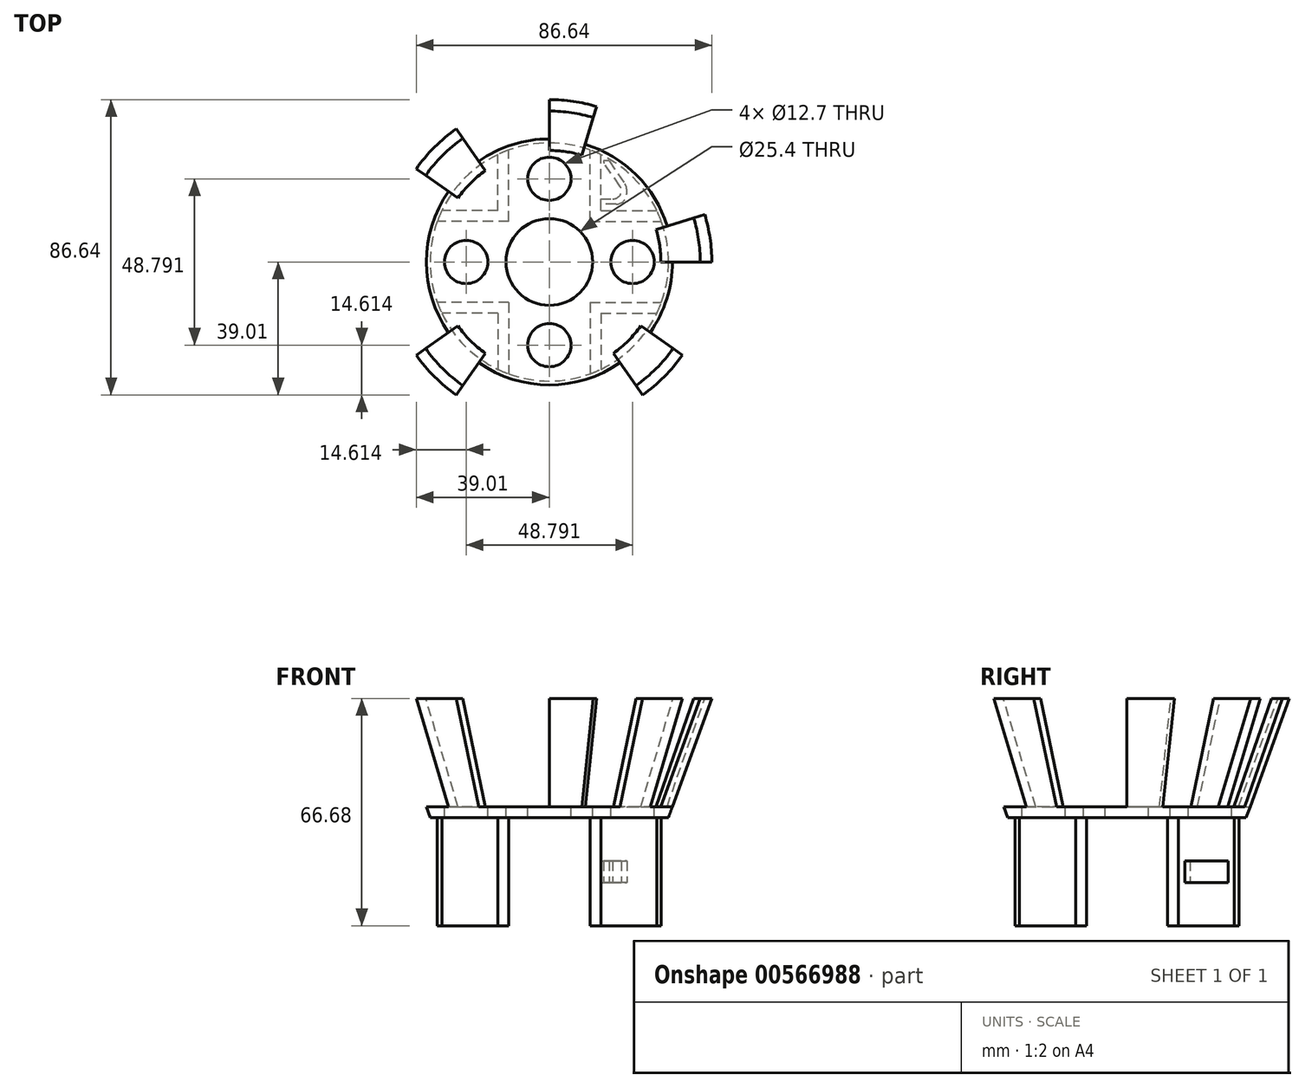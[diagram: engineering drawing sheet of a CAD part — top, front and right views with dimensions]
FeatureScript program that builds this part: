
annotation { "Feature Type Name" : "Feature", "Feature Type Description" : "" }
export const myFeature = defineFeature(function(context is Context, id is Id, definition is map)
    precondition{}
    {
        {
            var Q0;
            Q0=qCreatedBy(makeId("Front.planeOp"),FACE);
            var sketch = newSketch(context, id + "F0", { "sketchPlane" : qUnion([Q0])});
            skLineSegment(sketch, "E0", {"start": v(0, 0) * mm, "end": v(-34.93, 0) * mm});
            skLineSegment(sketch, "E1", {"start": v(-34.92, 0) * mm, "end": v(-47.62, 34.92) * mm});
            skLineSegment(sketch, "E2", {"start": v(-47.63, 34.93) * mm, "end": v(0, 34.93) * mm});
            skLineSegment(sketch, "E3", {"start": v(0, 34.93) * mm, "end": v(0, 0) * mm});
            skSolve(sketch);
        }
        {
            var Q0;
            Q0=qCreatedBy(makeId("Front.planeOp"),FACE);
            var sketch = newSketch(context, id + "F1", { "sketchPlane" : qUnion([Q0])});
            skLineSegment(sketch, "E4", {"start": v(0, 0) * mm, "end": v(0, 48.8) * mm, "construction": true});
            skSolve(sketch);
        }
        {
            var Q0;
            Q0=makeQuery(id+"F0.imprint","IMPRINT",FACE,{"disambiguationData":[TD([[makeQuery(id+"F0.imprint","IMPRINT",EDGE,{"derivedFrom":sQuery(id+"F0.wireOp",EDGE,"E0")}),-1.0]])]});
            var Q1;
            Q1=sQuery(id+"F1.wireOp",EDGE,"E4");
            revolve(context, id + "F2", {"entities" : qUnion([Q0]), "axis" : qUnion([Q1]), "revolveType" : RevolveType.FULL});
        }
        {
            var Q0;
            Q0=makeQuery(id+"F2.opRevolve","SWEPT_FACE",FACE,{"disambiguationData":[OSD([sQuery(id+"F0.wireOp",EDGE,"E2")])]});
            shell(context, id + "F3", {"entities" : qUnion([Q0]), "thickness" : 3.17 * mm});
        }
        {
            var Q0;
            Q0=makeQuery(id+"F2.opRevolve","SWEPT_FACE",FACE,{"disambiguationData":[OSD([sQuery(id+"F0.wireOp",EDGE,"E0")])]});
            var sketch = newSketch(context, id + "F4", { "sketchPlane" : qUnion([Q0])});
            skLineSegment(sketch, "E5", {"start": v(0, 0) * mm, "end": v(0, 34.93) * mm, "construction": true});
            skLineSegment(sketch, "E6", {"start": v(0, 0) * mm, "end": v(-34.93, 0) * mm, "construction": true});
            skLineSegment(sketch, "E7", {"start": v(-11.9, 11.9) * mm, "end": v(-32.83, 11.9) * mm});
            skLineSegment(sketch, "E8", {"start": v(-11.9, 11.9) * mm, "end": v(-11.9, 32.83) * mm});
            skLineSegment(sketch, "E9", {"start": v(-15.08, 15.08) * mm, "end": v(-31.5, 15.08) * mm});
            skLineSegment(sketch, "E10", {"start": v(-15.08, 15.08) * mm, "end": v(-15.08, 31.5) * mm});
            skLineSegment(sketch, "E11.1.0", {"start": v(-11.9, -11.9) * mm, "end": v(-32.83, -11.9) * mm});
            skLineSegment(sketch, "E11.1.1", {"start": v(-11.9, -11.9) * mm, "end": v(-11.9, -32.83) * mm});
            skLineSegment(sketch, "E11.1.2", {"start": v(-15.08, -15.08) * mm, "end": v(-31.5, -15.08) * mm});
            skLineSegment(sketch, "E11.1.3", {"start": v(-15.08, -15.08) * mm, "end": v(-15.08, -31.5) * mm});
            skLineSegment(sketch, "E11.2.0", {"start": v(11.9, -11.9) * mm, "end": v(11.9, -32.83) * mm});
            skLineSegment(sketch, "E11.2.1", {"start": v(11.9, -11.9) * mm, "end": v(32.83, -11.9) * mm});
            skLineSegment(sketch, "E11.2.2", {"start": v(15.08, -15.08) * mm, "end": v(15.08, -31.5) * mm});
            skLineSegment(sketch, "E11.2.3", {"start": v(15.08, -15.08) * mm, "end": v(31.5, -15.08) * mm});
            skLineSegment(sketch, "E11.3.0", {"start": v(11.9, 11.9) * mm, "end": v(32.83, 11.9) * mm});
            skLineSegment(sketch, "E11.3.1", {"start": v(11.9, 11.9) * mm, "end": v(11.9, 32.83) * mm});
            skLineSegment(sketch, "E11.3.2", {"start": v(15.08, 15.08) * mm, "end": v(31.5, 15.08) * mm});
            skLineSegment(sketch, "E11.3.3", {"start": v(15.08, 15.08) * mm, "end": v(15.08, 31.5) * mm});
            skPoint(sketch, "E11.center", {"position": v(0, 0) * mm});
            skArc(sketch, "E12", {"start": v(-31.5, 15.08) * mm, "mid": v(-32.2, 13.51) * mm, "end": v(-32.83, 11.9) * mm});
            skArc(sketch, "E13.trimOffspring", {"start": v(-11.9, 32.83) * mm, "mid": v(-13.51, 32.2) * mm, "end": v(-15.08, 31.5) * mm});
            skArc(sketch, "E14.trimOffspring", {"start": v(15.08, 31.5) * mm, "mid": v(13.51, 32.2) * mm, "end": v(11.9, 32.83) * mm});
            skArc(sketch, "E15.trimOffspring", {"start": v(-32.83, -11.9) * mm, "mid": v(-32.2, -13.51) * mm, "end": v(-31.5, -15.08) * mm});
            skArc(sketch, "E16.trimOffspring", {"start": v(-15.08, -31.5) * mm, "mid": v(-13.51, -32.2) * mm, "end": v(-11.9, -32.83) * mm});
            skArc(sketch, "E17.trimOffspring", {"start": v(11.9, -32.83) * mm, "mid": v(13.51, -32.2) * mm, "end": v(15.08, -31.5) * mm});
            skArc(sketch, "E18.trimOffspring", {"start": v(31.5, -15.08) * mm, "mid": v(32.2, -13.51) * mm, "end": v(32.83, -11.9) * mm});
            skArc(sketch, "E19.trimOffspring", {"start": v(32.83, 11.9) * mm, "mid": v(32.2, 13.51) * mm, "end": v(31.5, 15.08) * mm});
            skSolve(sketch);
        }
        {
            var Q0;
            Q0 = qSketchRegion(id + "F4", true);
            extrude(context, id + "F5", {"entities" : qUnion([Q0]), "operationType" : NewBodyOperationType.ADD, "depth" : 31.75 * mm, "offsetDistance" : 25.4 * mm});
        }
        {
            var Q0;
            Q0=makeQuery(id+"F2.opRevolve","SWEPT_FACE",FACE,{"disambiguationData":[OSD([sQuery(id+"F0.wireOp",EDGE,"E2")])]});
            var sketch = newSketch(context, id + "F6", { "sketchPlane" : qUnion([Q0])});
            skLineSegment(sketch, "E20", {"start": v(0, 0) * mm, "end": v(15.72, 51.64) * mm});
            skLineSegment(sketch, "E21", {"start": v(0, 0) * mm, "end": v(51.64, 15.72) * mm});
            skLineSegment(sketch, "E22", {"start": v(0, 0) * mm, "end": v(43.98, 43.98) * mm, "construction": true});
            skPoint(sketch, "E23", {"position": v(33.68, 33.68) * mm});
            skLineSegment(sketch, "E24", {"start": v(33.68, 33.68) * mm, "end": v(51.64, 15.72) * mm});
            skLineSegment(sketch, "E25", {"start": v(33.68, 33.68) * mm, "end": v(15.72, 51.64) * mm});
            skPoint(sketch, "E26.orphan", {"position": v(69.6, -2.25) * mm});
            skSolve(sketch);
        }
        {
            var Q0;
            Q0 = qSketchRegion(id + "F6", true);
            var Q1;
            Q1=makeQuery(id+"F3.opShell","OFFSET_FACE",FACE,{"disambiguationData":[OSD([sQuery(id+"F0.wireOp",EDGE,"E0")])]});
            extrude(context, id + "F7", {"entities" : qUnion([Q0]), "operationType" : NewBodyOperationType.REMOVE, "endBound" : BoundingType.UP_TO_SURFACE, "oppositeDirection" : true, "depth" : 25.4 * mm, "endBoundEntityFace" : qUnion([Q1]), "offsetDistance" : 25.4 * mm});
        }
        {
            var Q0;
            Q0=makeQuery(id+"F2.opRevolve","SWEPT_FACE",FACE,{"disambiguationData":[OSD([sQuery(id+"F0.wireOp",EDGE,"E2")])]});
            var sketch = newSketch(context, id + "F8", { "sketchPlane" : qUnion([Q0])});
            skLineSegment(sketch, "E27", {"start": v(0, 0) * mm, "end": v(0, 47.62) * mm});
            skLineSegment(sketch, "E28", {"start": v(0, 0) * mm, "end": v(47.62, 0) * mm});
            skLineSegment(sketch, "E29", {"start": v(0, 0) * mm, "end": v(-33.68, 33.68) * mm, "construction": true});
            skLineSegment(sketch, "E30", {"start": v(0, 0) * mm, "end": v(33.68, -33.68) * mm, "construction": true});
            skLineSegment(sketch, "E31", {"start": v(0, 0) * mm, "end": v(-33.68, -33.68) * mm, "construction": true});
            skLineSegment(sketch, "E32", {"start": v(0, 0) * mm, "end": v(-27.32, 39.01) * mm});
            skLineSegment(sketch, "E33", {"start": v(0, 0) * mm, "end": v(-39.01, 27.32) * mm});
            skLineSegment(sketch, "E34.1.0", {"start": v(0, 0) * mm, "end": v(-27.32, -39.01) * mm});
            skLineSegment(sketch, "E34.1.1", {"start": v(0, 0) * mm, "end": v(-39.01, -27.32) * mm});
            skLineSegment(sketch, "E34.2.0", {"start": v(0, 0) * mm, "end": v(39.01, -27.32) * mm});
            skLineSegment(sketch, "E34.2.1", {"start": v(0, 0) * mm, "end": v(27.32, -39.01) * mm});
            skPoint(sketch, "E34.center", {"position": v(0, 0) * mm});
            skArc(sketch, "E35", {"start": v(-39.01, 27.32) * mm, "mid": v(-47.62, 0) * mm, "end": v(-39.01, -27.32) * mm});
            skArc(sketch, "E36.trimOffspring", {"start": v(0, 47.62) * mm, "mid": v(-14.32, 45.42) * mm, "end": v(-27.32, 39.01) * mm});
            skArc(sketch, "E37.trimOffspring", {"start": v(-27.32, -39.01) * mm, "mid": v(0, -47.62) * mm, "end": v(27.32, -39.01) * mm});
            skArc(sketch, "E38.trimOffspring", {"start": v(39.01, -27.32) * mm, "mid": v(45.42, -14.32) * mm, "end": v(47.62, 0) * mm});
            skSolve(sketch);
        }
        {
            var Q0;
            Q0 = qSketchRegion(id + "F8", true);
            var Q1;
            Q1=makeQuery(id+"F7.boolean.opBoolean","MERGE",FACE,{"derivedFrom":[makeQuery(id+"F3.opShell","OFFSET_FACE",FACE,{"disambiguationData":[OSD([sQuery(id+"F0.wireOp",EDGE,"E0")])]})],"fromTools":[makeQuery(id+"F7.opExtrude","CAP_FACE",FACE,{"disambiguationData":[OSD([sQuery(id+"F6.wireOp",EDGE,"E20"),sQuery(id+"F6.wireOp",EDGE,"E21"),sQuery(id+"F6.wireOp",EDGE,"E24"),sQuery(id+"F6.wireOp",EDGE,"E25")])],"isStart":false})]});
            extrude(context, id + "F9", {"entities" : qUnion([Q0]), "operationType" : NewBodyOperationType.REMOVE, "endBound" : BoundingType.UP_TO_SURFACE, "oppositeDirection" : true, "depth" : 25.4 * mm, "endBoundEntityFace" : qUnion([Q1]), "offsetDistance" : 25.4 * mm});
        }
        {
            var Q0;
            Q0=makeQuery(id+"F9.boolean.opBoolean","MERGE",FACE,{"derivedFrom":[makeQuery(id+"F7.boolean.opBoolean","MERGE",FACE,{"derivedFrom":[makeQuery(id+"F3.opShell","OFFSET_FACE",FACE,{"disambiguationData":[OSD([sQuery(id+"F0.wireOp",EDGE,"E0")])]})],"fromTools":[makeQuery(id+"F7.opExtrude","CAP_FACE",FACE,{"disambiguationData":[OSD([sQuery(id+"F6.wireOp",EDGE,"E20"),sQuery(id+"F6.wireOp",EDGE,"E21"),sQuery(id+"F6.wireOp",EDGE,"E24"),sQuery(id+"F6.wireOp",EDGE,"E25")])],"isStart":false})]})],"fromTools":[makeQuery(id+"F9.opExtrude","CAP_FACE",FACE,{"disambiguationData":[OSD([sQuery(id+"F8.wireOp",EDGE,"E27"),sQuery(id+"F8.wireOp",EDGE,"E32"),sQuery(id+"F8.wireOp",EDGE,"E36.trimOffspring")])],"isStart":false}),makeQuery(id+"F9.opExtrude","CAP_FACE",FACE,{"disambiguationData":[OSD([sQuery(id+"F8.wireOp",EDGE,"E28"),sQuery(id+"F8.wireOp",EDGE,"E34.2.0"),sQuery(id+"F8.wireOp",EDGE,"E38.trimOffspring")])],"isStart":false}),makeQuery(id+"F9.opExtrude","CAP_FACE",FACE,{"disambiguationData":[OSD([sQuery(id+"F8.wireOp",EDGE,"E33"),sQuery(id+"F8.wireOp",EDGE,"E34.1.1"),sQuery(id+"F8.wireOp",EDGE,"E35")])],"isStart":false}),makeQuery(id+"F9.opExtrude","CAP_FACE",FACE,{"disambiguationData":[OSD([sQuery(id+"F8.wireOp",EDGE,"E34.1.0"),sQuery(id+"F8.wireOp",EDGE,"E34.2.1"),sQuery(id+"F8.wireOp",EDGE,"E37.trimOffspring")])],"isStart":false})]});
            var sketch = newSketch(context, id + "F10", { "sketchPlane" : qUnion([Q0])});
            skCircle(sketch, "E39", {"center": v(0, 0) * mm, "radius": 12.7 * mm});
            skSolve(sketch);
        }
        {
            var Q0;
            Q0 = qSketchRegion(id + "F10", true);
            extrude(context, id + "F11", {"entities" : qUnion([Q0]), "operationType" : NewBodyOperationType.REMOVE, "oppositeDirection" : true, "depth" : 25.4 * mm, "offsetDistance" : 25.4 * mm});
        }
        {
            var Q0;
            Q0=makeQuery(id+"F5.opExtrude","SWEPT_FACE",FACE,{"disambiguationData":[OSD([sQuery(id+"F4.wireOp",EDGE,"E11.2.2")])]});
            var sketch = newSketch(context, id + "F12", { "sketchPlane" : qUnion([Q0])});
            skLineSegment(sketch, "E40", {"start": v(31.5, -15.88) * mm, "end": v(15.08, -15.88) * mm, "construction": true});
            skLineSegment(sketch, "E41.bottom", {"start": v(16.94, -19.05) * mm, "end": v(29.64, -19.05) * mm});
            skLineSegment(sketch, "E41.top", {"start": v(16.94, -12.7) * mm, "end": v(29.64, -12.7) * mm});
            skLineSegment(sketch, "E41.left", {"start": v(16.94, -19.05) * mm, "end": v(16.94, -12.7) * mm});
            skLineSegment(sketch, "E41.right", {"start": v(29.64, -19.05) * mm, "end": v(29.64, -12.7) * mm});
            skPoint(sketch, "E41.middle", {"position": v(23.3, -15.88) * mm});
            skSolve(sketch);
        }
        {
            var Q0;
            Q0 = qSketchRegion(id + "F12", true);
            extrude(context, id + "F13", {"entities" : qUnion([Q0]), "operationType" : NewBodyOperationType.ADD, "depth" : 7.62 * mm, "offsetDistance" : 25.4 * mm});
        }
        {
            var Q0;
            Q0=makeQuery(id+"F13.opExtrude","SWEPT_FACE",FACE,{"disambiguationData":[OSD([sQuery(id+"F12.wireOp",EDGE,"E41.bottom")])]});
            var sketch = newSketch(context, id + "F14", { "sketchPlane" : qUnion([Q0])});
            skArc(sketch, "E42", {"start": v(20.7, -22.18) * mm, "mid": v(20.8, -19.7) * mm, "end": v(18.6, -18.54) * mm});
            skLineSegment(sketch, "E43", {"start": v(20.7, -22.18) * mm, "end": v(16.12, -28.89) * mm});
            skLineSegment(sketch, "E44", {"start": v(15.89, -29.64) * mm, "end": v(15.89, -29.64) * mm});
            skLineSegment(sketch, "E45", {"start": v(17.53, -29.64) * mm, "end": v(22.15, -22.89) * mm});
            skLineSegment(sketch, "E46", {"start": v(22.7, -21.1) * mm, "end": v(22.7, -20.12) * mm});
            skLineSegment(sketch, "E47", {"start": v(19.53, -16.94) * mm, "end": v(15.08, -16.94) * mm});
            skLineSegment(sketch, "E48", {"start": v(15.08, -18.54) * mm, "end": v(18.6, -18.54) * mm});
            skPoint(sketch, "E49.visualSharp", {"position": v(22.7, -16.94) * mm});
            skArc(sketch, "E49.filletArc", {"start": v(22.7, -20.12) * mm, "mid": v(21.77, -17.87) * mm, "end": v(19.53, -16.94) * mm});
            skPoint(sketch, "E50.visualSharp", {"position": v(22.7, -22.08) * mm});
            skArc(sketch, "E50.filletArc", {"start": v(22.15, -22.89) * mm, "mid": v(22.56, -22.03) * mm, "end": v(22.7, -21.1) * mm});
            skPoint(sketch, "E51.visualSharp", {"position": v(15.89, -29.23) * mm});
            skArc(sketch, "E51.filletArc", {"start": v(16.12, -28.89) * mm, "mid": v(15.95, -29.25) * mm, "end": v(15.89, -29.64) * mm});
            skLineSegment(sketch, "E52.bottom", {"start": v(22.7, -29.64) * mm, "end": v(17.53, -29.64) * mm});
            skLineSegment(sketch, "E52.top", {"start": v(22.7, -16.94) * mm, "end": v(15.08, -16.94) * mm});
            skLineSegment(sketch, "E52.left", {"start": v(22.7, -29.64) * mm, "end": v(22.7, -16.94) * mm});
            skLineSegment(sketch, "E52.right", {"start": v(15.08, -29.64) * mm, "end": v(15.08, -18.54) * mm});
            skLineSegment(sketch, "E53.trimOffspring", {"start": v(15.89, -29.64) * mm, "end": v(15.08, -29.64) * mm});
            skSolve(sketch);
        }
        {
            var Q0;
            Q0 = qSketchRegion(id + "F14", true);
            extrude(context, id + "F15", {"entities" : qUnion([Q0]), "operationType" : NewBodyOperationType.REMOVE, "endBound" : BoundingType.UP_TO_NEXT, "oppositeDirection" : true, "depth" : 25.4 * mm, "offsetDistance" : 25.4 * mm});
        }
        {
            var Q0;
            Q0=makeQuery(id+"F9.boolean.opBoolean","MERGE",FACE,{"derivedFrom":[makeQuery(id+"F7.boolean.opBoolean","MERGE",FACE,{"derivedFrom":[makeQuery(id+"F3.opShell","OFFSET_FACE",FACE,{"disambiguationData":[OSD([sQuery(id+"F0.wireOp",EDGE,"E0")])]})],"fromTools":[makeQuery(id+"F7.opExtrude","CAP_FACE",FACE,{"disambiguationData":[OSD([sQuery(id+"F6.wireOp",EDGE,"E20"),sQuery(id+"F6.wireOp",EDGE,"E21"),sQuery(id+"F6.wireOp",EDGE,"E24"),sQuery(id+"F6.wireOp",EDGE,"E25")])],"isStart":false})]})],"fromTools":[makeQuery(id+"F9.opExtrude","CAP_FACE",FACE,{"disambiguationData":[OSD([sQuery(id+"F8.wireOp",EDGE,"E27"),sQuery(id+"F8.wireOp",EDGE,"E32"),sQuery(id+"F8.wireOp",EDGE,"E36.trimOffspring")])],"isStart":false}),makeQuery(id+"F9.opExtrude","CAP_FACE",FACE,{"disambiguationData":[OSD([sQuery(id+"F8.wireOp",EDGE,"E28"),sQuery(id+"F8.wireOp",EDGE,"E34.2.0"),sQuery(id+"F8.wireOp",EDGE,"E38.trimOffspring")])],"isStart":false}),makeQuery(id+"F9.opExtrude","CAP_FACE",FACE,{"disambiguationData":[OSD([sQuery(id+"F8.wireOp",EDGE,"E33"),sQuery(id+"F8.wireOp",EDGE,"E34.1.1"),sQuery(id+"F8.wireOp",EDGE,"E35")])],"isStart":false}),makeQuery(id+"F9.opExtrude","CAP_FACE",FACE,{"disambiguationData":[OSD([sQuery(id+"F8.wireOp",EDGE,"E34.1.0"),sQuery(id+"F8.wireOp",EDGE,"E34.2.1"),sQuery(id+"F8.wireOp",EDGE,"E37.trimOffspring")])],"isStart":false})]});
            var sketch = newSketch(context, id + "F16", { "sketchPlane" : qUnion([Q0])});
            skCircle(sketch, "E54", {"center": v(-24.4, 0) * mm, "radius": 6.35 * mm});
            skPoint(sketch, "E54.centerSnap0", {"position": v(-36.08, 0) * mm});
            skCircle(sketch, "E55.1.0", {"center": v(0, -24.4) * mm, "radius": 6.35 * mm});
            skCircle(sketch, "E55.2.0", {"center": v(24.4, 0) * mm, "radius": 6.35 * mm});
            skCircle(sketch, "E55.3.0", {"center": v(0, 24.4) * mm, "radius": 6.35 * mm});
            skPoint(sketch, "E55.center", {"position": v(0, 0) * mm});
            skSolve(sketch);
        }
        {
            var Q0;
            Q0 = qSketchRegion(id + "F16", true);
            extrude(context, id + "F17", {"entities" : qUnion([Q0]), "operationType" : NewBodyOperationType.REMOVE, "oppositeDirection" : true, "depth" : 25.4 * mm, "offsetDistance" : 25.4 * mm});
        }
    });
